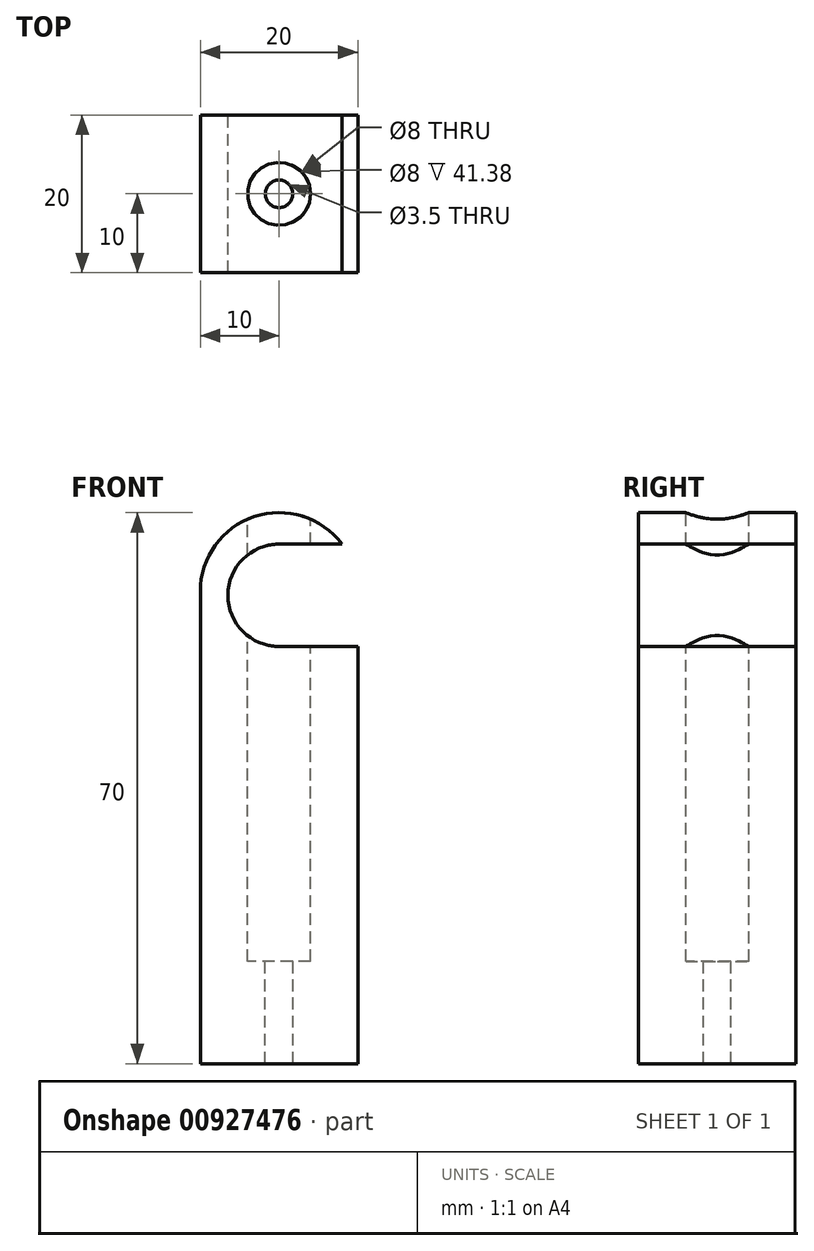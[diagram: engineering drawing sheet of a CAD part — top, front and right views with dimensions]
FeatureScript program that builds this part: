
annotation { "Feature Type Name" : "Feature", "Feature Type Description" : "" }
export const myFeature = defineFeature(function(context is Context, id is Id, definition is map)
    precondition{}
    {
        {
            var Q0;
            Q0=qCreatedBy(makeId("Front.planeOp"),FACE);
            var sketch = newSketch(context, id + "F0", { "sketchPlane" : qUnion([Q0])});
            skLineSegment(sketch, "E0", {"start": v(-10, 60) * mm, "end": v(-10, 0) * mm});
            skLineSegment(sketch, "E1", {"start": v(-10, 0) * mm, "end": v(10, 0) * mm});
            skLineSegment(sketch, "E2", {"start": v(10, 0) * mm, "end": v(10, 60) * mm});
            skArc(sketch, "E3", {"start": v(10, 60) * mm, "mid": v(0, 70) * mm, "end": v(-10, 60) * mm});
            skSolve(sketch);
        }
        {
            var Q0;
            Q0 = qSketchRegion(id + "F0", true);
            extrude(context, id + "F1", {"entities" : qUnion([Q0]), "depth" : 10 * mm, "offsetDistance" : 25 * mm, "hasSecondDirection" : true, "secondDirectionOppositeDirection" : true, "secondDirectionDepth" : 10 * mm});
        }
        {
            var Q0;
            Q0=makeQuery(id+"F1.opExtrude","CAP_FACE",FACE,{"disambiguationData":[OSD([sQuery(id+"F0.wireOp",EDGE,"E0"),sQuery(id+"F0.wireOp",EDGE,"E1"),sQuery(id+"F0.wireOp",EDGE,"E2"),sQuery(id+"F0.wireOp",EDGE,"E3")])],"isStart":true});
            var sketch = newSketch(context, id + "F2", { "sketchPlane" : qUnion([Q0])});
            skArc(sketch, "E4", {"start": v(0, 53) * mm, "mid": v(6.5, 59.5) * mm, "end": v(0, 66) * mm});
            skLineSegment(sketch, "E5", {"start": v(0, 53) * mm, "end": v(-10, 53) * mm});
            skLineSegment(sketch, "E6", {"start": v(-10, 53) * mm, "end": v(-10, 66) * mm});
            skLineSegment(sketch, "E7", {"start": v(-10, 66) * mm, "end": v(0, 66) * mm});
            skSolve(sketch);
        }
        {
            var Q0;
            {var subQ5=sQuery(id+"F2.wireOp",EDGE,"E4");Q0=makeQuery(id+"F2.imprint","IMPRINT",FACE,{"disambiguationData":[TD([[makeQuery(id+"F2.imprint","IMPRINT",EDGE,{"derivedFrom":subQ5}),1.0]])]});}
            var Q1;
            Q1=makeQuery(id+"F1.opExtrude","CAP_FACE",FACE,{"disambiguationData":[OSD([sQuery(id+"F0.wireOp",EDGE,"E0"),sQuery(id+"F0.wireOp",EDGE,"E1"),sQuery(id+"F0.wireOp",EDGE,"E2"),sQuery(id+"F0.wireOp",EDGE,"E3")])],"isStart":false});
            extrude(context, id + "F3", {"entities" : qUnion([Q0]), "operationType" : NewBodyOperationType.REMOVE, "endBound" : BoundingType.UP_TO_SURFACE, "oppositeDirection" : true, "depth" : 25 * mm, "endBoundEntityFace" : qUnion([Q1]), "offsetDistance" : 25 * mm});
        }
        {
            var Q0;
            Q0=makeQuery(id+"F3.boolean.opBoolean","COPY",FACE,{"derivedFrom":makeQuery(id+"F3.opExtrude","SWEPT_FACE",FACE,{"disambiguationData":[OSD([sQuery(id+"F2.wireOp",EDGE,"E5")])]})});
            var sketch = newSketch(context, id + "F4", { "sketchPlane" : qUnion([Q0])});
            skCircle(sketch, "E8", {"center": v(0, 0) * mm, "radius": 4 * mm});
            skSolve(sketch);
        }
        {
            var Q0;
            Q0 = qSketchRegion(id + "F4", true);
            var Q1;
            Q1=makeQuery(id+"F1.opExtrude","SWEPT_FACE",FACE,{"disambiguationData":[OSD([sQuery(id+"F0.wireOp",EDGE,"E3")])]});
            extrude(context, id + "F5", {"entities" : qUnion([Q0]), "operationType" : NewBodyOperationType.REMOVE, "oppositeDirection" : true, "depth" : 40 * mm, "offsetDistance" : 25 * mm, "hasSecondDirection" : true, "secondDirectionBound" : SecondDirectionBoundingType.UP_TO_SURFACE, "secondDirectionOppositeDirection" : false, "secondDirectionDepth" : 25 * mm, "secondDirectionBoundEntityFace" : qUnion([Q1])});
        }
        {
            var Q0;
            {var subQ0=sQuery(id+"F4.wireOp",EDGE,"E8");var subQ1=makeQuery(id+"F3.boolean.opBoolean","COPY",EDGE,{"derivedFrom":makeQuery(id+"F3.opExtrude","SWEPT_EDGE",EDGE,{"disambiguationData":[OSD([sQuery(id+"F2.wireOp",EDGE,"E4"),sQuery(id+"F2.wireOp",EDGE,"E5")])]})});var subQ2=makeQuery(id+"F4.imprint","INTERSECT",VERTEX,{"disambiguationData":[OD(0.0)],"derivedFrom":[subQ1,subQ0]});Q0=makeQuery(id+"F5.boolean.opBoolean","COPY",FACE,{"derivedFrom":makeQuery(id+"F5.opExtrude","CAP_FACE",FACE,{"disambiguationData":[OSD([subQ0]),topologyDisambiguationEdgeConnected([makeQuery(id+"F4.imprint","IMPRINT",EDGE,{"disambiguationData":[TD([[subQ2,-1.0]])],"derivedFrom":subQ0})])],"isStart":false})});}
            var sketch = newSketch(context, id + "F6", { "sketchPlane" : qUnion([Q0])});
            skPoint(sketch, "E9", {"position": v(0, 0) * mm});
            skSolve(sketch);
        }
        {
            var Q0;
            Q0=sQuery(id+"F6.wireOp",VERTEX,"E9");
            var Q1;
            Q1=makeQuery(id+"F1.opExtrude","SWEPT_BODY",BODY,{"disambiguationData":[OSD([sQuery(id+"F0.wireOp",EDGE,"E0"),sQuery(id+"F0.wireOp",EDGE,"E1"),sQuery(id+"F0.wireOp",EDGE,"E2"),sQuery(id+"F0.wireOp",EDGE,"E3")])]});
            hole(context, id + "F7", {"style" : HoleStyle.SIMPLE, "endStyle" : HoleEndStyle.THROUGH, "holeDiameter" : 3.5 * mm, "majorDiameter" : 5 * mm, "isTappedThrough" : true, "tappedDepth" : 12 * mm, "tapClearance" : 3, "locations" : qUnion([Q0]), "scope" : qUnion([Q1])});
        }
    });
